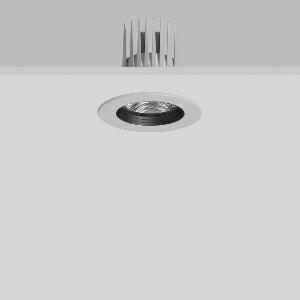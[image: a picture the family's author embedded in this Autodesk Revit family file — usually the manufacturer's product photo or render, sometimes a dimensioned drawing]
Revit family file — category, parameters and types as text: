
# Revit family: heledon_mini_e_901742_004_76_ff52
name_source: partatom
category: Lighting Fixtures
units: mm (PartAtom-declared; Revit-internal decimal feet)

## family parameters
Cut with Voids When Loaded = No
Host = Face
Light Source = No
Part Type = Normal
Room Calculation Point = No
Round Connector Dimension = Use Diameter
Shared = No

## types (1)
- HELEDON mini E (1 x LED Modul 930, 2550 lm, 3000)
    Apparent Load = 20 VA
    Approval mark = CE
    CIE Flux Codes = 95 99 100 100 100
    Color Rendering = 90
    Color Temperature = 3000
    Default Elevation = 1800 mm
    Description = Series: HELEDON mini
Round recessed downlight. Housing: die-cast aluminium, powder-coated. Black plastic ring and recessed LED to prevent glare from the side. Optical assembly with reflector made of MIRO-Silver with 98% total light reflection for outstanding efficiency - can be changed without tools. Best colour rendering index Ra>90. Suitable for Recessed ceiling mounting. Installation without tools thanks to spring fastening system. Including separate LED converter with connecting cable 600 mm.High quality converter without flickering and stroboscopic effect. Through-wiring box (5 pole) available as accessory. The following accessories can be mounted without use of tools: interchangeable lenses, decorative glasses, honeycomb louvre, clear and frosted diffusers, white interchangeable plastic ring. 
Colour: silver
Diameter: 124 mm
Height: 3 mm
Cut-out diameter: 114 mm
Recess height: 170 mm
Luminaire: recess height: 120 mm
Lamp: LED
Socket: without socket
Colour temperature: 3000K
Colour rendering index (CRI): 92
System power: 20 W
Rated luminous flux: 2550 lm
Luminous efficiency: 128 lm/W
Control gear: Converter, dimmable, DALI
Protection class: II
Type of protection: IP 20
    Height = 0 mm  [stored 0 ft]
    Lamp = 1 x LED Modul 930
    Lamp Light Flux = 2550 lm
    Lamp count = 1
    Length = 124 mm  [stored 0.406824 ft]
    Lifetime = 50000 h
    Luminous efficacy = 128 lm/W
    Manufacturer = RZB
    ModVariant = No
    Model = 901742.004.76
    Mounting Place = Ceiling
    Mounting Type = Recessed
    Number of Poles = 1
    OnlyDefault = Yes
    Power Factor = 1
    Product Name = HELEDON mini E
    Product group = Recessed downlights
    ProductGroupID = 402
    Protection Class = Protection class II
    Protection Degree = IP 20
    RLX_Detail_Level = 1
    RLX_Emergency_Light_Flux = 0 lm
    RLX_Emergency_Type = 0
    RLX_Emergency_Type_DB = No
    RlxData = <blob elided: 128413 chars, md5=2a0cc84f>
    Socket = socket
    Standby Power = 0 W
    System Light Flux = 2550 lm
    System Power = 20 W
    Type Comments = Product without accessories
    Type Image = 901657.004.jpg
    URL = http://relux.com
    VarID = ---
    Voltage = 230 V
    Voltage Range = 220-240 V
    Weight = 0.00 kg
    Width = 0 mm  [stored 0 ft]

note: [stored X ft] marks values corroborated as IEEE doubles in the binary element streams (Revit-internal decimal feet)

## geometry (parser evidence)
native form markers: Blend x4, Sweep x12
no freeform markers — native parametric forms only
